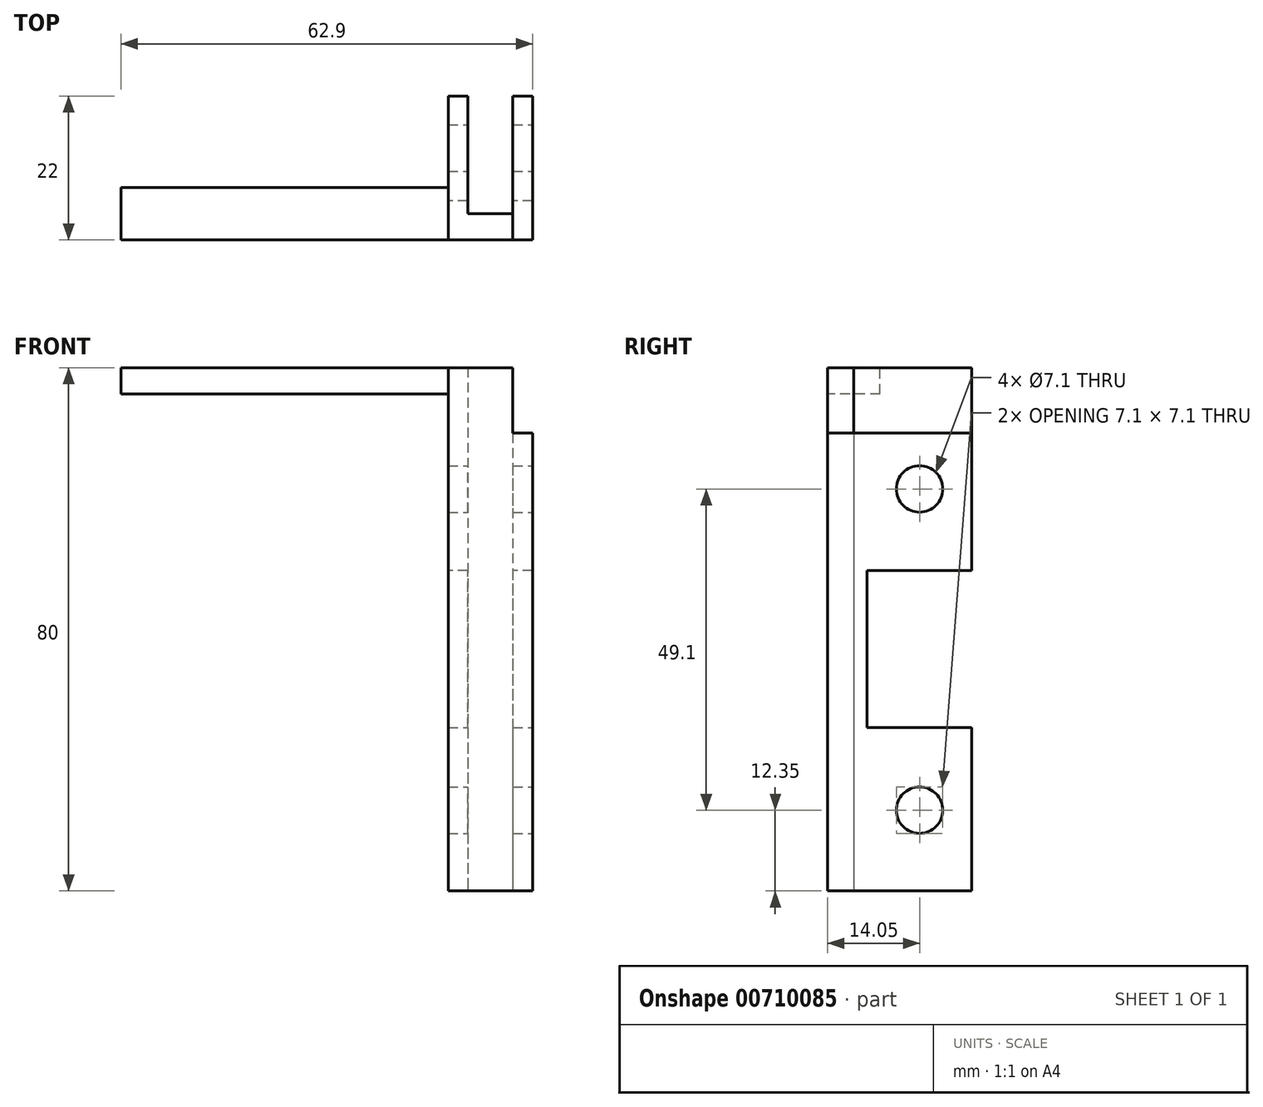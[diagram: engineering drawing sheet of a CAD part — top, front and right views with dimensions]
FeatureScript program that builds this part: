
annotation { "Feature Type Name" : "Feature", "Feature Type Description" : "" }
export const myFeature = defineFeature(function(context is Context, id is Id, definition is map)
    precondition{}
    {
        {
            var Q0;
            Q0=qCreatedBy(makeId("Top.planeOp"),FACE);
            var sketch = newSketch(context, id + "F0", { "sketchPlane" : qUnion([Q0])});
            skLineSegment(sketch, "E0", {"start": v(0, 0) * mm, "end": v(0, 22) * mm});
            skLineSegment(sketch, "E1", {"start": v(0, 22) * mm, "end": v(12.9, 22) * mm});
            skLineSegment(sketch, "E2", {"start": v(12.9, 22) * mm, "end": v(12.9, 0) * mm});
            skLineSegment(sketch, "E3", {"start": v(12.9, 0) * mm, "end": v(0, 0) * mm});
            skLineSegment(sketch, "E4", {"start": v(3, 22) * mm, "end": v(3, 4) * mm});
            skLineSegment(sketch, "E5", {"start": v(3, 4) * mm, "end": v(9.9, 4) * mm});
            skLineSegment(sketch, "E6", {"start": v(9.9, 4) * mm, "end": v(9.9, 22) * mm});
            skSolve(sketch);
        }
        {
            var Q0;
            {var subQ3=sQuery(id+"F0.wireOp",EDGE,"E0");Q0=makeQuery(id+"F0.imprint","IMPRINT",FACE,{"disambiguationData":[TD([[makeQuery(id+"F0.imprint","IMPRINT",EDGE,{"derivedFrom":subQ3}),-1.0]])]});}
            extrude(context, id + "F1", {"entities" : qUnion([Q0]), "depth" : 70 * mm, "offsetDistance" : 25 * mm});
        }
        {
            var Q0;
            Q0=makeQuery(id+"F1.opExtrude","SWEPT_FACE",FACE,{"disambiguationData":[OSD([sQuery(id+"F0.wireOp",EDGE,"E2")])]});
            var sketch = newSketch(context, id + "F2", { "sketchPlane" : qUnion([Q0])});
            skCircle(sketch, "E7", {"center": v(14.05, 61.45) * mm, "radius": 3.55 * mm});
            skCircle(sketch, "E8", {"center": v(14.05, 12.35) * mm, "radius": 3.55 * mm});
            skSolve(sketch);
        }
        {
            var Q0;
            Q0=makeQuery(id+"F2.imprint","IMPRINT",FACE,{"disambiguationData":[TD([[makeQuery(id+"F2.imprint","IMPRINT",EDGE,{"derivedFrom":sQuery(id+"F2.wireOp",EDGE,"E7")}),1.0]])]});
            var Q1;
            Q1=makeQuery(id+"F2.imprint","IMPRINT",FACE,{"disambiguationData":[TD([[makeQuery(id+"F2.imprint","IMPRINT",EDGE,{"derivedFrom":sQuery(id+"F2.wireOp",EDGE,"E8")}),1.0]])]});
            extrude(context, id + "F3", {"entities" : qUnion([Q0, Q1]), "operationType" : NewBodyOperationType.REMOVE, "endBound" : BoundingType.THROUGH_ALL, "oppositeDirection" : true, "depth" : 25 * mm, "offsetDistance" : 25 * mm});
        }
        {
            var Q0;
            Q0=makeQuery(id+"F1.opExtrude","CAP_FACE",FACE,{"disambiguationData":[OSD([sQuery(id+"F0.wireOp",EDGE,"E0"),sQuery(id+"F0.wireOp",EDGE,"E1"),sQuery(id+"F0.wireOp",EDGE,"E2"),sQuery(id+"F0.wireOp",EDGE,"E3"),sQuery(id+"F0.wireOp",EDGE,"E4"),sQuery(id+"F0.wireOp",EDGE,"E5"),sQuery(id+"F0.wireOp",EDGE,"E6")])],"isStart":false});
            var sketch = newSketch(context, id + "F4", { "sketchPlane" : qUnion([Q0])});
            skLineSegment(sketch, "E9", {"start": v(9.9, 4) * mm, "end": v(9.9, 0) * mm});
            skPoint(sketch, "E9.endSnap0", {"position": v(6.45, 0) * mm});
            skSolve(sketch);
        }
        {
            var Q0;
            {var subQ4=sQuery(id+"F4.wireOp",EDGE,"E9");Q0=makeQuery(id+"F4.imprint","IMPRINT",FACE,{"disambiguationData":[TD([[makeQuery(id+"F4.imprint","IMPRINT",EDGE,{"derivedFrom":subQ4}),-1.0]])]});}
            extrude(context, id + "F5", {"entities" : qUnion([Q0]), "operationType" : NewBodyOperationType.ADD, "depth" : 10 * mm, "offsetDistance" : 25 * mm});
        }
        {
            var Q0;
            {var subQ0=sQuery(id+"F0.wireOp",EDGE,"E0");Q0=makeQuery(id+"F5.boolean.opBoolean","MERGE",FACE,{"derivedFrom":[makeQuery(id+"F1.opExtrude","SWEPT_FACE",FACE,{"disambiguationData":[OSD([subQ0])]}),makeQuery(id+"F5.opExtrude","SWEPT_FACE",FACE,{"disambiguationData":[OSD([subQ0])]})]});}
            var sketch = newSketch(context, id + "F6", { "sketchPlane" : qUnion([Q0])});
            skLineSegment(sketch, "E10", {"start": v(-22, 76) * mm, "end": v(0, 76) * mm});
            skLineSegment(sketch, "E11", {"start": v(-8, 76) * mm, "end": v(-8, 80) * mm});
            skLineSegment(sketch, "E12", {"start": v(-8, 80) * mm, "end": v(0, 80) * mm});
            skLineSegment(sketch, "E13", {"start": v(0, 80) * mm, "end": v(0, 76) * mm});
            skSolve(sketch);
        }
        {
            var Q0;
            {var subQ4=sQuery(id+"F6.wireOp",EDGE,"E11");Q0=makeQuery(id+"F6.imprint","IMPRINT",FACE,{"disambiguationData":[TD([[makeQuery(id+"F6.imprint","IMPRINT",EDGE,{"derivedFrom":subQ4}),-1.0]])]});}
            extrude(context, id + "F7", {"entities" : qUnion([Q0]), "depth" : 50 * mm, "offsetDistance" : 25 * mm});
        }
        {
            var Q0;
            {var subQ0=sQuery(id+"F0.wireOp",EDGE,"E1");Q0=makeQuery(id+"F1.opExtrude","SWEPT_FACE",FACE,{"disambiguationData":[OSD([subQ0]),TDD([makeQuery(id+"F0.imprint","IMPRINT",EDGE,{"disambiguationData":[TD([[makeQuery(id+"F0.imprint","INTERSECT",VERTEX,{"derivedFrom":[subQ0,sQuery(id+"F0.wireOp",EDGE,"E2")]}),1.0]])],"derivedFrom":subQ0})])]});}
            var sketch = newSketch(context, id + "F8", { "sketchPlane" : qUnion([Q0])});
            skLineSegment(sketch, "E14", {"start": v(-12.9, 49) * mm, "end": v(0, 49) * mm});
            skLineSegment(sketch, "E15", {"start": v(0, 49) * mm, "end": v(0, 25) * mm});
            skLineSegment(sketch, "E16", {"start": v(0, 25) * mm, "end": v(-12.9, 25) * mm});
            skLineSegment(sketch, "E17", {"start": v(-12.9, 25) * mm, "end": v(-12.9, 49) * mm});
            skSolve(sketch);
        }
        {
            var Q0;
            Q0=makeQuery(id+"F8.imprint","IMPRINT",FACE,{"disambiguationData":[TD([[makeQuery(id+"F8.imprint","IMPRINT",EDGE,{"derivedFrom":sQuery(id+"F8.wireOp",EDGE,"vN7vXV1M-gyVh-wu98-0U4N-jEQqpl8zVVec")}),1.0]])]});
            var Q1;
            {var subQ0=sQuery(id+"F8.wireOp",EDGE,"E15");Q1=makeQuery(id+"F8.imprint","IMPRINT",FACE,{"disambiguationData":[TD([[makeQuery(id+"F8.imprint","IMPRINT",EDGE,{"derivedFrom":subQ0}),-1.0]])]});}
            var Q2;
            {var subQ0=sQuery(id+"F8.wireOp",EDGE,"E17");Q2=makeQuery(id+"F8.imprint","IMPRINT",FACE,{"disambiguationData":[TD([[makeQuery(id+"F8.imprint","IMPRINT",EDGE,{"derivedFrom":subQ0}),1.0]])]});}
            extrude(context, id + "F9", {"entities" : qUnion([Q0, Q1, Q2]), "operationType" : NewBodyOperationType.REMOVE, "oppositeDirection" : true, "depth" : 16 * mm, "offsetDistance" : 25 * mm});
        }
    });
